# Revit family: York CB-ABV-YK - Vertical Recessed Active Chilled Beam,Generic,Revit 2015 R1.1
name_source: partatom
category: Mechanical Equipment
revit_build: Autodesk Revit 2015 (Build: 20160512_1515(x64)
units: mm (PartAtom-declared; Revit-internal decimal feet)

## types (1)
- CB-ABV-YK
    (0) Front and Back Supply = Yes
    (1) Front Supply = No
    (2) Back Supply = No
    0 - No Insulation = Yes
    2 Ft = Yes
    26 - White = Yes
    2P1C - 2 Pipe Coil = Yes
    3 Ft = No
    4 Ft = No
    4 Pipe Visible = No
    4" Dia. = Yes
    4P1C - 4 Pipe Coil = No
    5" Dia. = No
    6 Ft = No
    6" Oval Inlet = No
    8 Ft = No
    8" Oval Inlet = No
    84 - Black Paint = No
    A = 20"
    Angle = 270.00°
    B = 21"
    B1 = Yes
    B2 = No
    B3 = No
    B4 = No
    C = 3 7/8"
    Chilled Water Connection Diameter = 0"
    Clearance Material = Clearance
    D = 5 7/8"
    Default Elevation = 48"
    Description = Vertical Recessed Active Chilled Beam
    H12 - SS Flex Hose - 12 inch = No
    H18 - SS Flex Hose - 18 inch = No
    H24 - SS Flex Hose - 24 inch = No
    Heating Water Connection Diameter = 0"
    L - Left Hand = Yes
    L - ½ in Ecosheild (Foil Face) = No
    MPT - Male Pipe Thread = No
    Manufacturer = York
    Material = Casing:  G90 20GA Galvanealed sheet metal
    Max Flow = 0 CFM
    Min Flow = 0 CFM
    Model = CB-ABV-YK, 2 - Pipe Coil, Left Hand
    Mounting Bracket = Yes
    Neck Size = 0"
    R - Right Hand = No
    SWT - Sweat = Yes
    Select a Nominal Beam Length = 1
    Select a Pipe Connection Type = 1
    Select a Plenum Liner (External) = 1
    Select a Water-Coil Connection Side = 1
    Select a Water-Coil Type = 1
    Select an Air Inlet Size = 1
    Select an Air Nozzle Configuration = 1
    URL = http://www.york.com
    Version = 2
    Water Connection Location Selection = 0

## geometry (parser evidence)
native form markers: Blend x2, Sweep x12
no freeform markers — native parametric forms only
